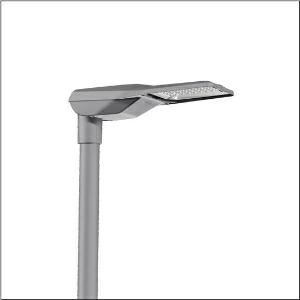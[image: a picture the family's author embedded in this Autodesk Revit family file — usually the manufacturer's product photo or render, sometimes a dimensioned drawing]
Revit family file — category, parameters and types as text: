
# Revit family: streetlight_sl_21_iq_mini___pl52_5xe2h31g08gb_d0f1
name_source: partatom
category: Lighting Fixtures
units: mm (PartAtom-declared; Revit-internal decimal feet)

## family parameters
Cut with Voids When Loaded = No
Host = Face
Light Source = No
Part Type = Normal
Room Calculation Point = No
Round Connector Dimension = Use Diameter
Shared = No

## types (1)
- --- (1 x LED, 5580 lm, 37.1 W, 3000K)
    Apparent Load = 37 VA
    CIE Flux Codes = 27 59 98 100 100
    Color Rendering = 70
    Color Temperature = 3000K
    Default Elevation = 1800 mm
    Description = Streetlight SL 21 iQ mini, mast luminaire, primary light control with lens, of PMMA, primary optical cover: cover, of toughened safety glass, transparent, light distribution: PL52, light emission: direct distribution, primary light characteristic: asymmetric, installation type: post-top, side-entry, LED, High Power LED, rated luminous flux: 5.580lm, luminous efficacy: 150lm/W, light colour: 730, colour temperature: 3000K, control: Street-Remote, Auto-Match, Temp-Guard, Lumen-Switch, Night-Set, Smart-Wire, Light-Fading, Desk-Remote (wireless, voltage-free reading and setting of iQ features in the workshop via application-optimized NFC function/RFID function), optimised constant luminous flux control (CLO 2.0), presetting dimming linear, mains connection: 220..240V, AC, 50/60Hz, start of lifetime: 37W, end of service life: 39W, reduction: 18W, luminaire housing, of diecast aluminium, powder-coated, Siteco® metallic grey (DB 702S), corrosivity category C5 mid according to DIN EN ISO 12944, please order mast flange separately, inclination adjustable: 0°, 5°, 10°, 15°, sealing non-destructively replaceable, multi-level sealing system, length: 628mm, width: 235mm, height: 110mm, mast flange for spigot size: 42mm (side-entry): 5XC10008XM4, 60/48mm (side-entry/post-top): 5XC10108XM2, 76/60mm (side-entry/post-top): 5XC10108XM1, protection rating (complete): IP66, insulation class (complete): insulation class II (safety insulation), certification: CE, ENEC, ENEC+, VDE, impact resistance: IK09, permissible operating ambient temperature for outdoor applications: -40..+50°C, standard-compliant lighting for roads and squares, packaging unit: 1 piece

Light Distribution: PL52
    Height = 110 mm
    Lamp = 1 x LED
    Lamp Light Flux = 5580 lm
    Lamp Power = 37.1 W
    Lamp count = 1
    Length = 625 mm
    Luminous efficacy = 150 lm/W
    Manufacturer = Siteco
    ModVariant = No
    Model = 5XE2H31G08GB
    Number of Poles = 1
    OnlyDefault = Yes
    Power Factor = 1
    Product Name = Streetlight SL 21 iQ mini | PL52
    Product group = mast luminaire | pylon top
    ProductGroupID = 6100
    Protection Class = Protection class II
    Protection Degree = IP 66
    RLX_Detail_Level = 1
    RLX_Emergency_Light_Flux = 0 lm
    RLX_Emergency_Type = 0
    RLX_Emergency_Type_DB = No
    RlxData = <blob elided: 101873 chars, md5=c1d630ab>
    Socket = socket
    Standby Power = 0 W
    System Light Flux = 5580 lm
    System Power = 37 W
    Type Comments = factory setting: luminous flux: 100 % | dim-lin: 254 | 385 mA
    Type Image = l_1003519.jpg
    URL = http://relux.com
    VarID = @adj_142643
    Voltage = 0 V
    Weight = 0.00 kg
    Width = 234 mm

## geometry (parser evidence)
native form markers: Blend x4, Sweep x10
no freeform markers — native parametric forms only
